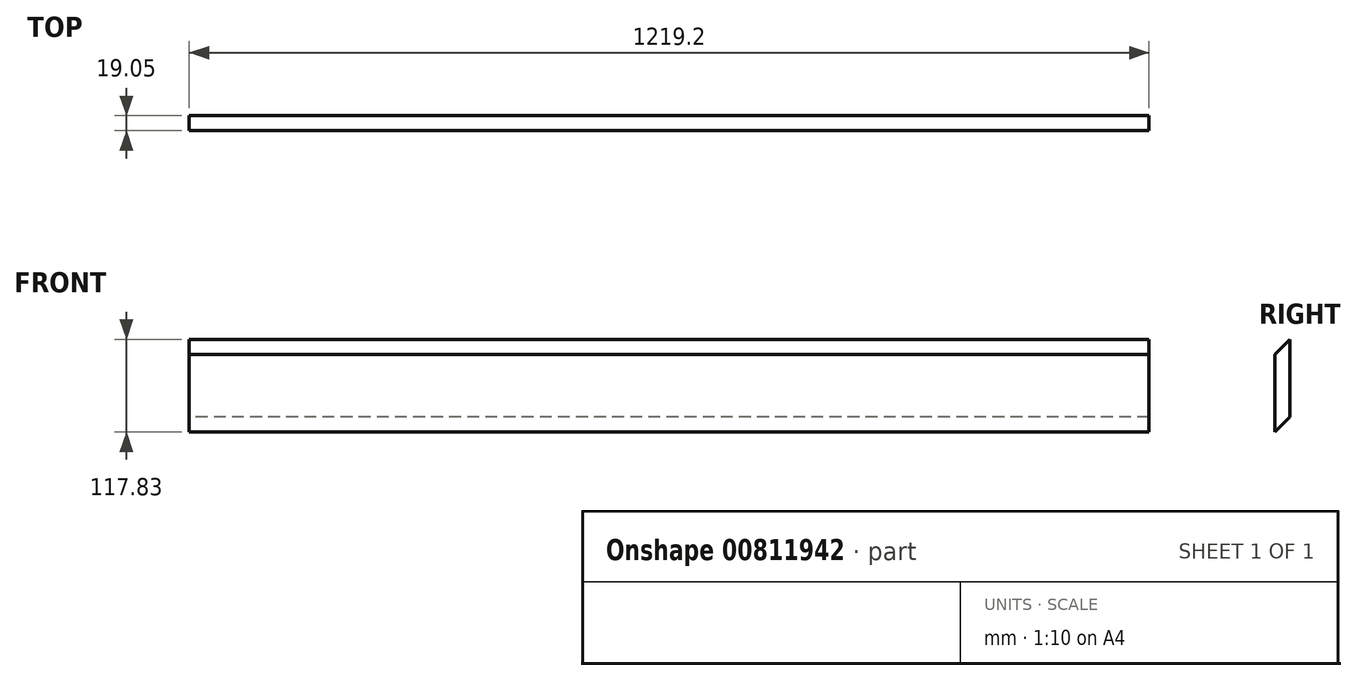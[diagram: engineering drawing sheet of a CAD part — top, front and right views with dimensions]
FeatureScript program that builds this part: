
annotation { "Feature Type Name" : "Feature", "Feature Type Description" : "" }
export const myFeature = defineFeature(function(context is Context, id is Id, definition is map)
    precondition{}
    {
        {
            var Q0;
            Q0=qCreatedBy(makeId("Right.planeOp"),FACE);
            var sketch = newSketch(context, id + "F0", { "sketchPlane" : qUnion([Q0])});
            skLineSegment(sketch, "E0", {"start": v(-19.05, 0) * mm, "end": v(0, 19.05) * mm});
            skLineSegment(sketch, "E1", {"start": v(-19.05, 0) * mm, "end": v(-19.05, 98.78) * mm});
            skLineSegment(sketch, "E2", {"start": v(0, 19.05) * mm, "end": v(0, 117.83) * mm});
            skLineSegment(sketch, "E3", {"start": v(-19.05, 98.78) * mm, "end": v(0, 117.83) * mm});
            skSolve(sketch);
        }
        {
            var Q0;
            Q0 = qSketchRegion(id + "F0", true);
            extrude(context, id + "F1", {"entities" : qUnion([Q0]), "depth" : 1219.2 * mm, "offsetDistance" : 25.4 * mm});
        }
    });
